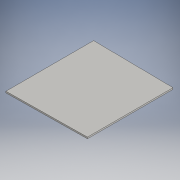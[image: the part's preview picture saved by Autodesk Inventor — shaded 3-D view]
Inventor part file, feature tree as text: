
AUTODESK INVENTOR PART (.ipt)
format: ipt  version: 2016 (Build 200138000, 138)  size: 89,088 bytes
history: native  units: in
note: dims shown in document units (in); Inventor stores cm internally (conversion verified against a paired STEP export)
features: extrude x1, sketch x1
ambient origin geometry x8: Origin, YZ Plane, XZ Plane, XY Plane, X Axis, Y Axis, Z Axis, Center Point
bodies: Solid1 (feature_tree)
feature tree (2):
  extrude  "Extrusion1"  Depth=0.625in
  sketch  "Sketch1"  dims[d0=35.625in d1=36.5in d2=33.5in d3=16.75in d4=0.625in d5=0.0in]
